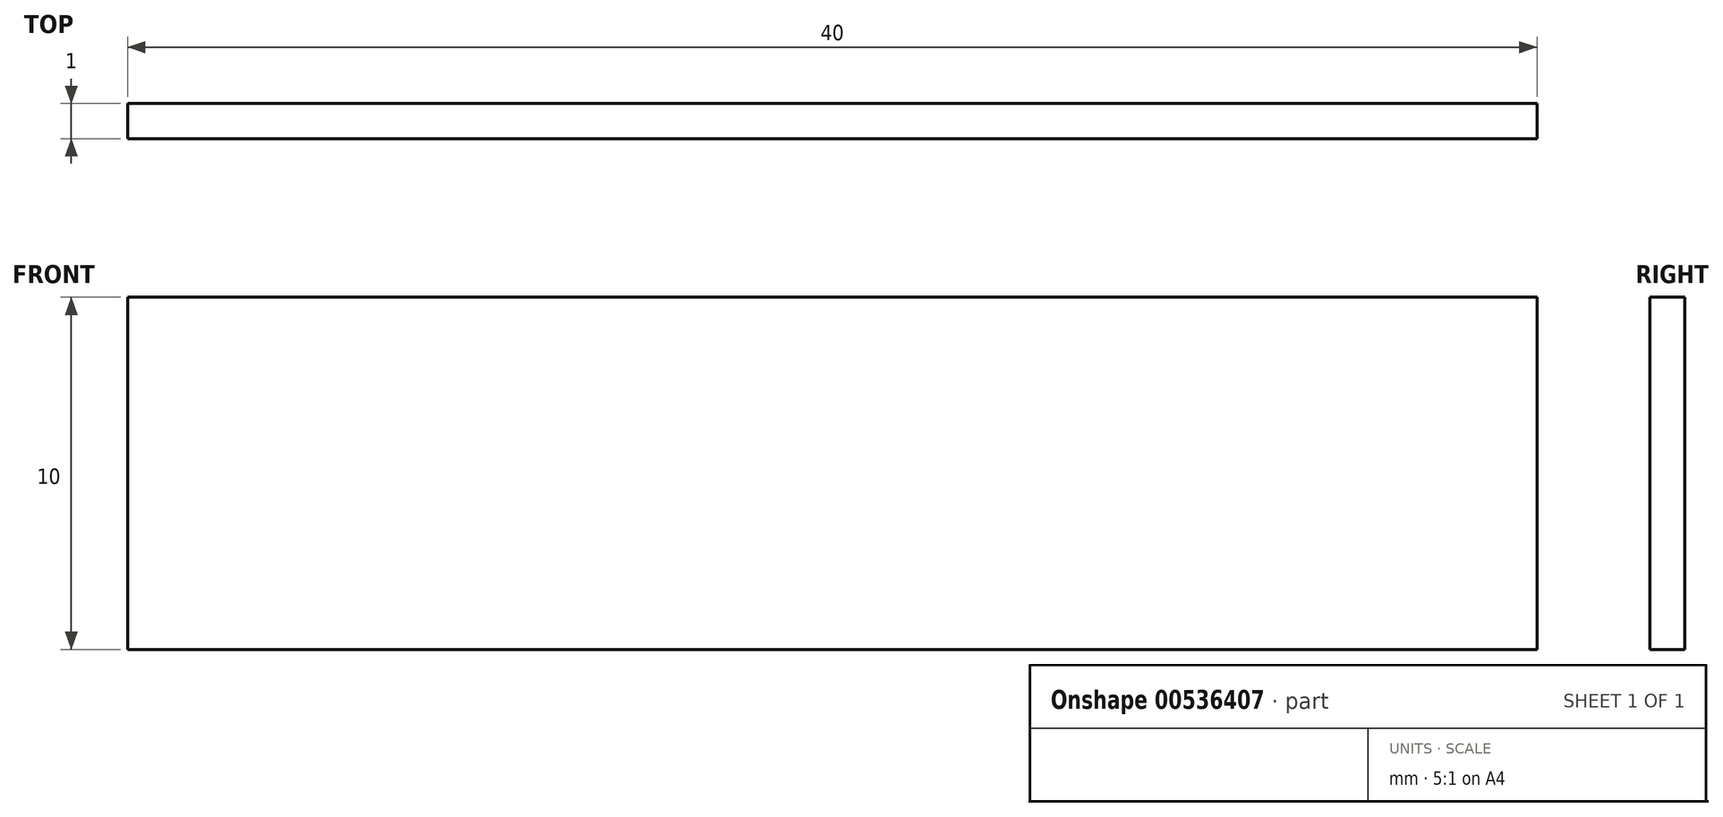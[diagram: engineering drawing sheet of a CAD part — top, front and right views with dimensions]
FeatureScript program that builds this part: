
annotation { "Feature Type Name" : "Feature", "Feature Type Description" : "" }
export const myFeature = defineFeature(function(context is Context, id is Id, definition is map)
    precondition{}
    {
        {
            var Q0;
            Q0=qCreatedBy(makeId("Front.planeOp"),FACE);
            var sketch = newSketch(context, id + "F0", { "sketchPlane" : qUnion([Q0])});
            skLineSegment(sketch, "E0.bottom", {"start": v(20, -5) * mm, "end": v(-20, -5) * mm});
            skLineSegment(sketch, "E0.top", {"start": v(20, 5) * mm, "end": v(-20, 5) * mm});
            skLineSegment(sketch, "E0.left", {"start": v(20, -5) * mm, "end": v(20, 5) * mm});
            skLineSegment(sketch, "E0.right", {"start": v(-20, -5) * mm, "end": v(-20, 5) * mm});
            skPoint(sketch, "E0.middle", {"position": v(0, 0) * mm});
            skSolve(sketch);
        }
        {
            var Q0;
            Q0=makeQuery(id+"F0.imprint","IMPRINT",FACE,{"disambiguationData":[TD([[makeQuery(id+"F0.imprint","IMPRINT",EDGE,{"derivedFrom":sQuery(id+"F0.wireOp",EDGE,"E0.bottom")}),-1.0]])]});
            extrude(context, id + "F1", {"entities" : qUnion([Q0]), "depth" : 1 * mm});
        }
    });
